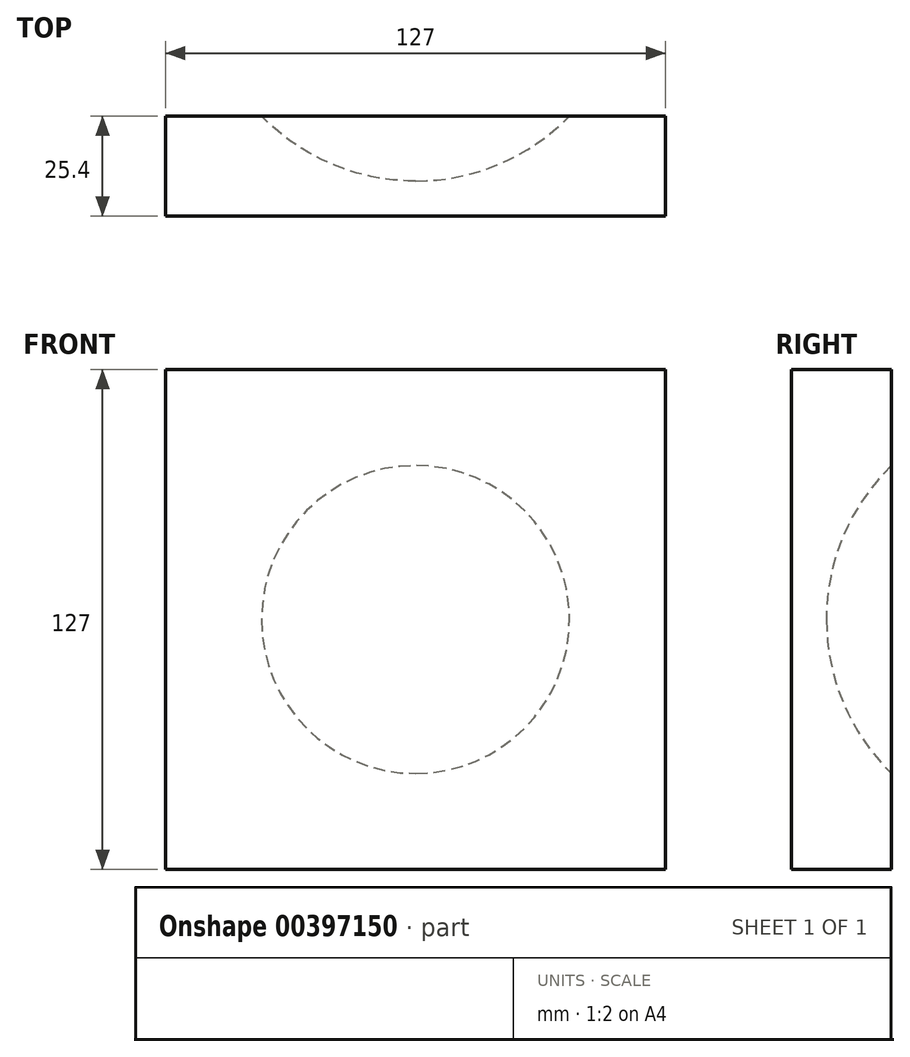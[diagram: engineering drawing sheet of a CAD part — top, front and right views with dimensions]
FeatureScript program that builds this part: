
annotation { "Feature Type Name" : "Feature", "Feature Type Description" : "" }
export const myFeature = defineFeature(function(context is Context, id is Id, definition is map)
    precondition{}
    {
        {
            var Q0;
            Q0=qCreatedBy(makeId("Front.planeOp"),FACE);
            var sketch = newSketch(context, id + "F0", { "sketchPlane" : qUnion([Q0])});
            skLineSegment(sketch, "E0.bottom", {"start": v(63.5, -63.5) * mm, "end": v(-63.5, -63.5) * mm});
            skLineSegment(sketch, "E0.top", {"start": v(63.5, 63.5) * mm, "end": v(-63.5, 63.5) * mm});
            skLineSegment(sketch, "E0.left", {"start": v(63.5, -63.5) * mm, "end": v(63.5, 63.5) * mm});
            skLineSegment(sketch, "E0.right", {"start": v(-63.5, -63.5) * mm, "end": v(-63.5, 63.5) * mm});
            skPoint(sketch, "E0.middle", {"position": v(0, 0) * mm});
            skSolve(sketch);
        }
        {
            var Q0;
            Q0 = qSketchRegion(id + "F0", true);
            extrude(context, id + "F1", {"entities" : qUnion([Q0]), "depth" : 25.4 * mm});
        }
        {
            var Q0;
            Q0=qCreatedBy(makeId("Top.planeOp"),FACE);
            var sketch = newSketch(context, id + "F2", { "sketchPlane" : qUnion([Q0])});
            skLineSegment(sketch, "E1", {"start": v(0, 0) * mm, "end": v(0, 38.1) * mm, "construction": true});
            skCircle(sketch, "E2", {"center": v(0, 38.1) * mm, "radius": 54.61 * mm});
            skLineSegment(sketch, "E3", {"start": v(0, -16.51) * mm, "end": v(0, 92.71) * mm});
            skSolve(sketch);
        }
        {
            var Q0;
            {var subQ0=sQuery(id+"F2.wireOp",EDGE,"E3");Q0=makeQuery(id+"F2.imprint","IMPRINT",FACE,{"disambiguationData":[TD([[makeQuery(id+"F2.imprint","IMPRINT",EDGE,{"derivedFrom":subQ0}),-1.0]])]});}
            var Q1;
            Q1=sQuery(id+"F2.wireOp",EDGE,"E3");
            revolve(context, id + "F3", {"operationType" : NewBodyOperationType.REMOVE, "entities" : qUnion([Q0]), "axis" : qUnion([Q1]), "revolveType" : RevolveType.FULL, "oppositeDirection" : true});
        }
    });
